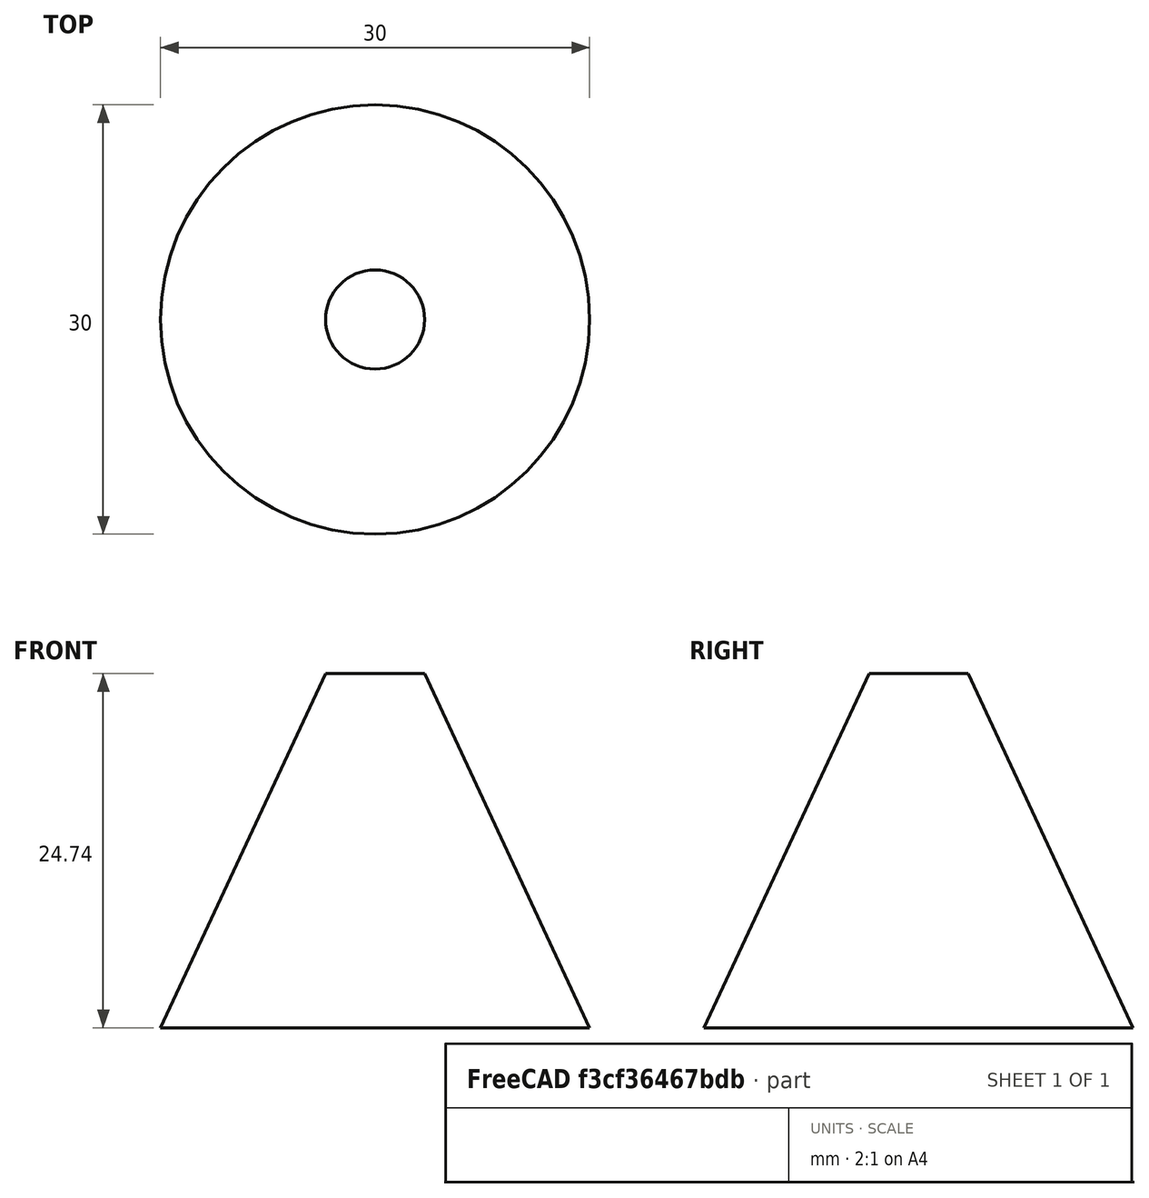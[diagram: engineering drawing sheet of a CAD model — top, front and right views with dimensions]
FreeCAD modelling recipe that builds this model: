
FCSTD DOCUMENT  (FreeCAD 1.0R38806 (Git))
Label: pieza_juego
License: All rights reserved
LicenseURL: https://en.wikipedia.org/wiki/All_rights_reserved
objects: Sketcher::SketchObject×1, Part::Revolution×1
note: 3 computed .brp shape members not serialized (recipe doc carries the construction recipe); baked Part::Feature solids carry a one-line shape summary decoded from their .brp

FEATURE [Sketcher::SketchObject] Sketch
  ArcFitTolerance = 1e-06
  FullyConstrained = false
  MakeInternals = false
  Placement = pos=(0,0,0) rot=(1,0,0;1.5708rad)
  sketch-geometry (4):
    g0: LineSegment StartX=1.3e-15 StartY=40 StartZ=0 EndX=0 EndY=0 EndZ=0
    g1: LineSegment StartX=0 StartY=0 StartZ=0 EndX=15 EndY=0 EndZ=0
    g2: LineSegment StartX=15 StartY=0 StartZ=0 EndX=3.46179 EndY=24.7438 EndZ=0
    g3: ArcOfCircle CenterX=0.094457 CenterY=32.0006 CenterZ=0 NormalX=0 NormalY=0 NormalZ=1 AngleXU=0 Radius=8 StartAngle=5.14684 EndAngle=7.86579
  constraints (11):
    c: PointOnObject(g0,g-2)
    c: Coincident(g0,g-1)
    c: DistanceY(g0,g0) = 40
    c: Coincident(g1,g0)
    c: PointOnObject(g1,g-1)
    c: DistanceX(g1,g1) = 15
    c: Coincident(g2,g1)
    c: Angle(g2,g1) = 1.13446
    c: Coincident(g3,g2)
    c: Coincident(g3,g0)
    c: Radius(g3) = 8
FEATURE [Part::Revolution] Revolve
  Angle = 360
  Axis = (0,0,1)
  Base = (0,0,0)
  FaceMakerClass = Part::FaceMakerBullseye
  Solid = true
  Source = -> Sketch
  Symmetric = false
